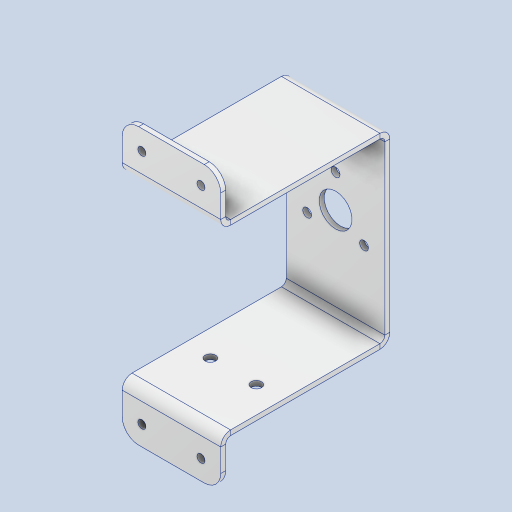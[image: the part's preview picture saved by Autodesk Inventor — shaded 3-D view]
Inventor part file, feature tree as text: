
AUTODESK INVENTOR PART (.ipt)
format: ipt  version: 2023 (Build 270158000, 158)  size: 236,544 bytes
history: native  units: mm
features: other x10, sketch x7, extrude x3, hole x1, fillet x1
ambient origin geometry x8: Origin, YZ Plane, XZ Plane, XY Plane, X Axis, Y Axis, Z Axis, Center Point
bodies: Body1 (feature_tree)
feature tree (22):
  other  "ソリッド1"
  other  "フランジ1"
  other  "フランジ2"
  extrude  "押し出し1"  Depth=30.0mm
  extrude  "押し出し3"  Depth=54.0mm
  hole  "穴1"  [1 undecoded]
  fillet  "フィレット1"  Radius=1.5mm
  extrude  "押し出し4"  Depth=0.75mm
  sketch  "スケッチ1"
  other  "プレート1"
  sketch  "スケッチ2"
  other  "プレート2"
  other  "曲げ1"
  other  "コーナー1"
  sketch  "スケッチ3"
  other  "プレート3"
  other  "曲げ2"
  other  "コーナー2"
  sketch  "スケッチ4"
  sketch  "スケッチ6"
  sketch  "スケッチ7"
  sketch  "スケッチ8"
note: 1 required parameter value undecoded (feature->parameter linkage not recoverable at this tier; creation-order binding heuristic only, values carry confidence <= 0.55)
